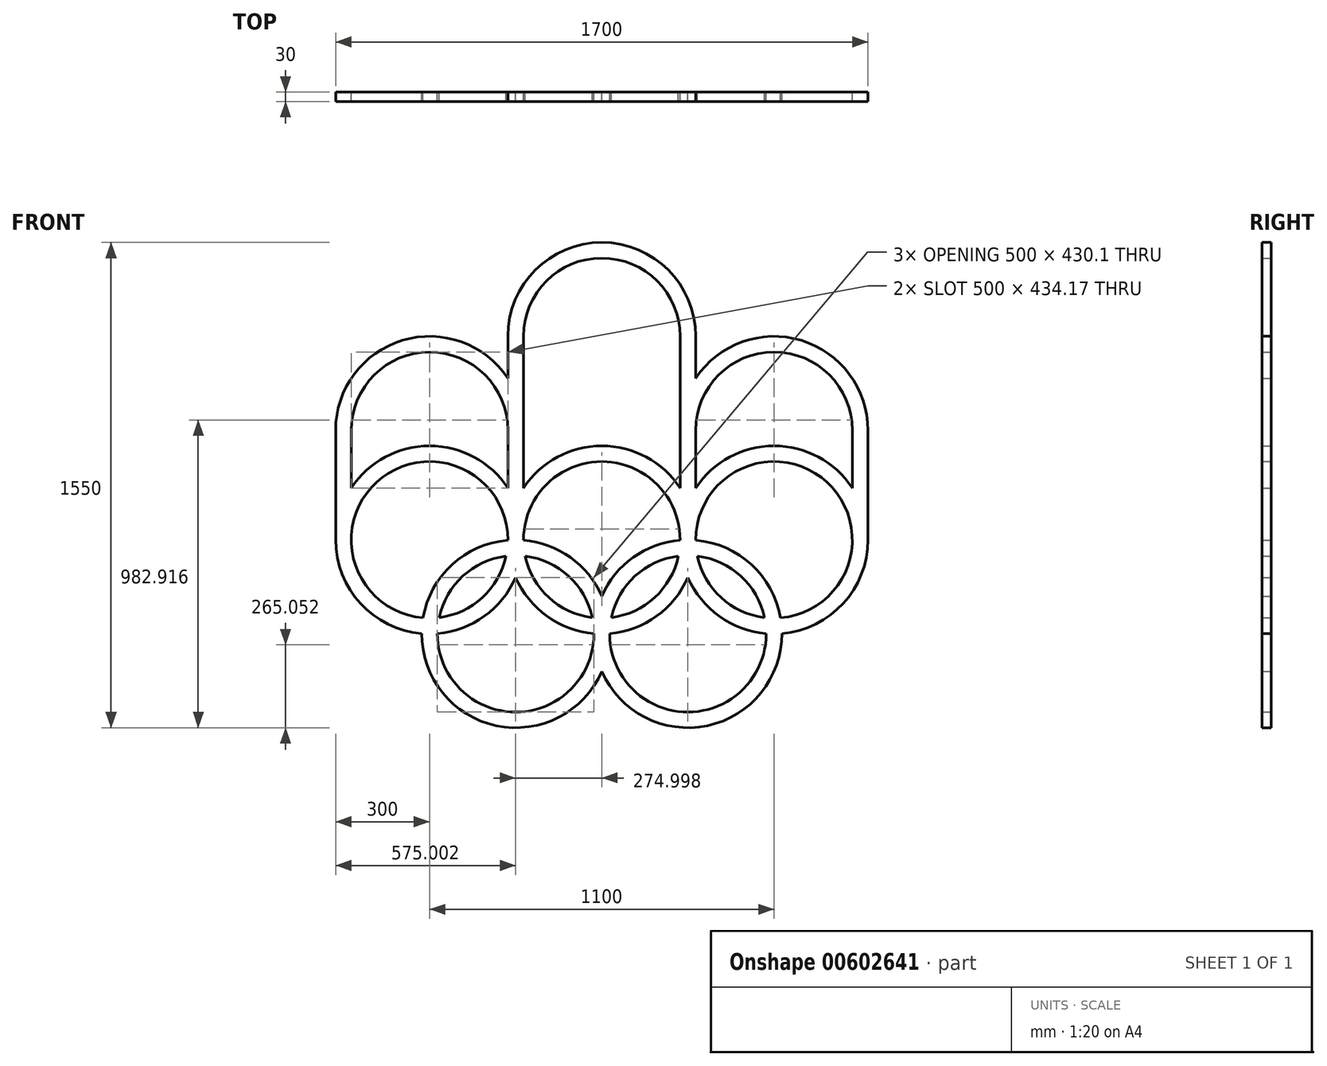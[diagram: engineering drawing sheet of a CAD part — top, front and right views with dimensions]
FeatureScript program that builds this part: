
annotation { "Feature Type Name" : "Feature", "Feature Type Description" : "" }
export const myFeature = defineFeature(function(context is Context, id is Id, definition is map)
    precondition{}
    {
        {
            var Q0;
            Q0=qCreatedBy(makeId("Front.planeOp"),FACE);
            var sketch = newSketch(context, id + "F0", { "sketchPlane" : qUnion([Q0])});
            skArc(sketch, "E0", {"start": v(-244.56, -51.86) * mm, "mid": v(-168.93, -184.29) * mm, "end": v(-30.44, -248.14) * mm});
            skArc(sketch, "E1", {"start": v(-275, -119.9) * mm, "mid": v(-174.69, -243.9) * mm, "end": v(-25, -298.96) * mm});
            skArc(sketch, "E2", {"start": v(305.44, -51.86) * mm, "mid": v(381.07, -184.29) * mm, "end": v(519.56, -248.14) * mm});
            skArc(sketch, "E3", {"start": v(275, -119.9) * mm, "mid": v(375.31, -243.9) * mm, "end": v(525, -298.96) * mm});
            skArc(sketch, "E4", {"start": v(-300, -1.04) * mm, "mid": v(-718.93, 184.29) * mm, "end": v(-570.66, -249.15) * mm});
            skArc(sketch, "E5", {"start": v(-850, 0) * mm, "mid": v(-770.8, -203.1) * mm, "end": v(-575, -298.96) * mm});
            skArc(sketch, "E6", {"start": v(-300, 350) * mm, "mid": v(-550, 600) * mm, "end": v(-800, 350) * mm});
            skLineSegment(sketch, "E7", {"start": v(-850, 350) * mm, "end": v(-850, 0) * mm});
            skLineSegment(sketch, "E8", {"start": v(-250, 350) * mm, "end": v(-250, 165.83) * mm});
            skLineSegment(sketch, "E9", {"start": v(-800, 350) * mm, "end": v(-800, 165.83) * mm});
            skLineSegment(sketch, "E10", {"start": v(-300, 350) * mm, "end": v(-300, 165.83) * mm});
            skArc(sketch, "E11.trimOffspring", {"start": v(-300, 515.83) * mm, "mid": v(-636.6, 637.23) * mm, "end": v(-850, 350) * mm});
            skArc(sketch, "E12.trimOffspring", {"start": v(-300, 165.83) * mm, "mid": v(-550, 300) * mm, "end": v(-800, 165.83) * mm});
            skArc(sketch, "E13", {"start": v(250, 650) * mm, "mid": v(0, 900) * mm, "end": v(-250, 650) * mm});
            skPoint(sketch, "E13.centerSnap0", {"position": v(-550, 650) * mm});
            skArc(sketch, "E14", {"start": v(300, 650) * mm, "mid": v(0, 950) * mm, "end": v(-300, 650) * mm});
            skLineSegment(sketch, "E15", {"start": v(-250, 650) * mm, "end": v(-250, 350) * mm});
            skLineSegment(sketch, "E16", {"start": v(-300, 650) * mm, "end": v(-300, 515.83) * mm});
            skArc(sketch, "E17", {"start": v(800, 350) * mm, "mid": v(550, 600) * mm, "end": v(300, 350) * mm});
            skLineSegment(sketch, "E18", {"start": v(850, 350) * mm, "end": v(850, 0) * mm});
            skLineSegment(sketch, "E19", {"start": v(250, 350) * mm, "end": v(250, 165.83) * mm});
            skLineSegment(sketch, "E20", {"start": v(300, 350) * mm, "end": v(300, 165.83) * mm});
            skLineSegment(sketch, "E21", {"start": v(800, 350) * mm, "end": v(800, 165.83) * mm});
            skLineSegment(sketch, "E22", {"start": v(300, 650) * mm, "end": v(300, 515.83) * mm});
            skLineSegment(sketch, "E23", {"start": v(250, 650) * mm, "end": v(250, 350) * mm});
            skArc(sketch, "E24.trimOffspring", {"start": v(250, 165.83) * mm, "mid": v(0, 300) * mm, "end": v(-250, 165.83) * mm});
            skArc(sketch, "E25.trimOffspring", {"start": v(850, 350) * mm, "mid": v(636.6, 637.23) * mm, "end": v(300, 515.83) * mm});
            skArc(sketch, "E26.trimOffspring", {"start": v(800, 165.83) * mm, "mid": v(550, 300) * mm, "end": v(300, 165.83) * mm});
            skArc(sketch, "E27", {"start": v(-305.44, -51.86) * mm, "mid": v(-443.93, -115.71) * mm, "end": v(-519.56, -248.14) * mm});
            skArc(sketch, "E28", {"start": v(-300, -1.04) * mm, "mid": v(-477.72, -78.85) * mm, "end": v(-570.66, -249.15) * mm});
            skPoint(sketch, "E29", {"position": v(-550, -300) * mm});
            skArc(sketch, "E30", {"start": v(25, -298.96) * mm, "mid": v(275, -550) * mm, "end": v(525, -298.96) * mm});
            skArc(sketch, "E31", {"start": v(0, -419.9) * mm, "mid": v(336.75, -593.58) * mm, "end": v(575, -298.96) * mm});
            skArc(sketch, "E32.trimOffspring", {"start": v(-519.56, -248.14) * mm, "mid": v(-381.07, -184.29) * mm, "end": v(-305.44, -51.86) * mm});
            skArc(sketch, "E33.trimOffspring", {"start": v(-525, -298.96) * mm, "mid": v(-275, -550) * mm, "end": v(-25, -298.96) * mm});
            skArc(sketch, "E34.trimOffspring", {"start": v(-575, -298.96) * mm, "mid": v(-336.75, -593.58) * mm, "end": v(0, -419.9) * mm});
            skArc(sketch, "E35.trimOffspring", {"start": v(-525, -298.96) * mm, "mid": v(-375.31, -243.9) * mm, "end": v(-275, -119.9) * mm});
            skArc(sketch, "E36.trimOffspring", {"start": v(25, -300) * mm, "mid": v(25, -299.48) * mm, "end": v(25, -298.96) * mm});
            skArc(sketch, "E37.trimOffspring", {"start": v(25, -298.96) * mm, "mid": v(174.69, -243.9) * mm, "end": v(275, -119.9) * mm});
            skArc(sketch, "E38.trimOffspring", {"start": v(-25, -298.96) * mm, "mid": v(-25, -299.48) * mm, "end": v(-25, -300) * mm});
            skArc(sketch, "E39.trimOffspring", {"start": v(0, -180.1) * mm, "mid": v(-100.31, -56.1) * mm, "end": v(-250, -1.04) * mm});
            skArc(sketch, "E40.trimOffspring", {"start": v(-30.44, -248.14) * mm, "mid": v(-106.07, -115.71) * mm, "end": v(-244.56, -51.86) * mm});
            skArc(sketch, "E41.trimOffspring", {"start": v(30.44, -248.14) * mm, "mid": v(168.93, -184.29) * mm, "end": v(244.56, -51.86) * mm});
            skArc(sketch, "E42.trimOffspring", {"start": v(244.56, -51.86) * mm, "mid": v(106.07, -115.71) * mm, "end": v(30.44, -248.14) * mm});
            skArc(sketch, "E43.trimOffspring", {"start": v(250, -1.04) * mm, "mid": v(100.31, -56.1) * mm, "end": v(0, -180.1) * mm});
            skArc(sketch, "E44.trimOffspring", {"start": v(250, -1.04) * mm, "mid": v(0, 250) * mm, "end": v(-250, -1.04) * mm});
            skArc(sketch, "E45.trimOffspring", {"start": v(570.66, -249.15) * mm, "mid": v(718.93, 184.29) * mm, "end": v(300, -1.04) * mm});
            skArc(sketch, "E46.trimOffspring", {"start": v(519.56, -248.14) * mm, "mid": v(443.93, -115.71) * mm, "end": v(305.44, -51.86) * mm});
            skArc(sketch, "E47.trimOffspring", {"start": v(570.66, -249.15) * mm, "mid": v(477.72, -78.85) * mm, "end": v(300, -1.04) * mm});
            skArc(sketch, "E48.trimOffspring", {"start": v(575, -298.96) * mm, "mid": v(770.8, -203.1) * mm, "end": v(850, 0) * mm});
            skSolve(sketch);
        }
        {
            var Q0;
            Q0 = qSketchRegion(id + "F0", true);
            extrude(context, id + "F1", {"entities" : qUnion([Q0]), "depth" : 30 * mm, "offsetDistance" : 25 * mm});
        }
    });
